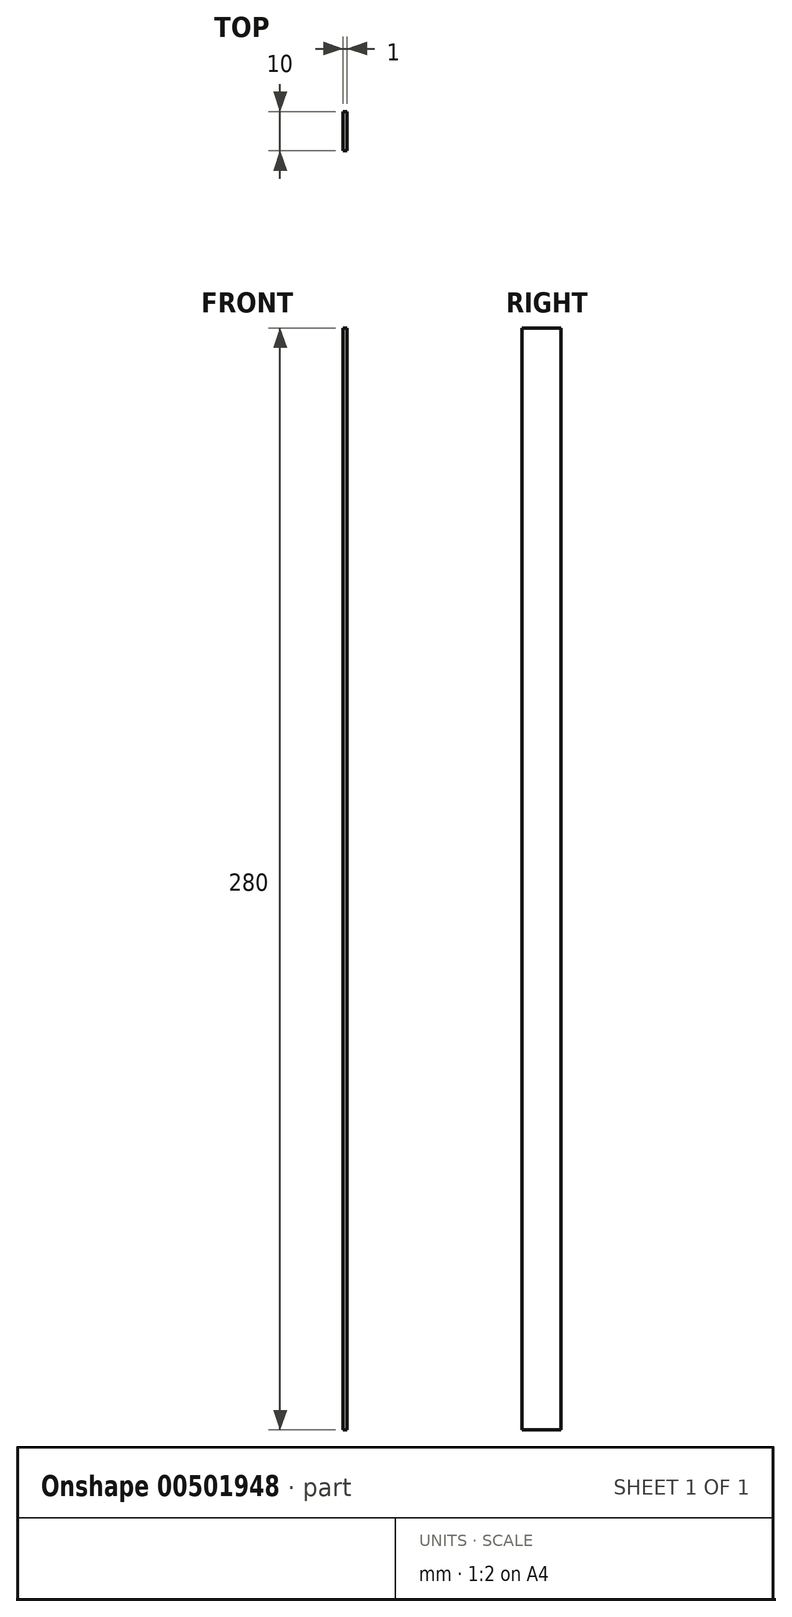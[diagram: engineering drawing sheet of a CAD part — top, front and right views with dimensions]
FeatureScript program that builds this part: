
annotation { "Feature Type Name" : "Feature", "Feature Type Description" : "" }
export const myFeature = defineFeature(function(context is Context, id is Id, definition is map)
    precondition{}
    {
        {
            var Q0;
            Q0=qCreatedBy(makeId("Right.planeOp"),FACE);
            var sketch = newSketch(context, id + "F0", { "sketchPlane" : qUnion([Q0])});
            skLineSegment(sketch, "E0.bottom", {"start": v(5, -140) * mm, "end": v(-5, -140) * mm});
            skLineSegment(sketch, "E0.top", {"start": v(5, 140) * mm, "end": v(-5, 140) * mm});
            skLineSegment(sketch, "E0.left", {"start": v(5, -140) * mm, "end": v(5, 140) * mm});
            skLineSegment(sketch, "E0.right", {"start": v(-5, -140) * mm, "end": v(-5, 140) * mm});
            skPoint(sketch, "E0.middle", {"position": v(0, 0) * mm});
            skSolve(sketch);
        }
        {
            var Q0;
            Q0 = qSketchRegion(id + "F0", true);
            extrude(context, id + "F1", {"entities" : qUnion([Q0]), "depth" : 1 * mm, "symmetric" : true});
        }
    });
